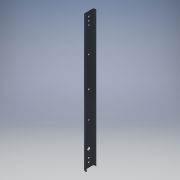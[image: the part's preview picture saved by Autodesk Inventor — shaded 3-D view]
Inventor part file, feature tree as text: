
AUTODESK INVENTOR PART (.ipt)
format: ipt  version: 2016 (Build 200138000, 138)  size: 188,416 bytes
history: native  units: mm
features: sketch x10, extrude x9, other x7, hole x1
ambient origin geometry x8: Origin, YZ Plane, XZ Plane, XY Plane, X Axis, Y Axis, Z Axis, Center Point
bodies: Solid1 (feature_tree)
feature tree (27):
  extrude  "Extrusion1"  Depth=0.5mm TaperAngle=0.0deg
  extrude  "Extrusion2"  Depth=0.5mm TaperAngle=0.0deg
  extrude  "Extrusion3"  Depth=0.5mm TaperAngle=0.0deg
  extrude  "Extrusion4"  Depth=0.5mm TaperAngle=0.0deg
  extrude  "Extrusion5"  [1 undecoded]
  extrude  "Extrusion6"  [1 undecoded]
  extrude  "Extrusion7"  [1 undecoded]
  extrude  "Extrusion8"  [1 undecoded]
  extrude  "Extrusion9"  [1 undecoded]
  hole  "Hole1"  [1 undecoded]
  other  "to_rail_XY"
  other  "to_rail_YZ"
  other  "to_rail_ZX"
  other  "to_rail_X"
  other  "to_rail_Y"
  other  "to_rail_Z"
  other  "to_rail_Center"
  sketch  "Sketch_1"  dims[d0=457.2mm d1=0.0mm d2=0.5mm d3=0.0mm]
  sketch  "Sketch_4"  dims[d8=0.5mm d9=0.0mm d10=0.5mm d11=0.0mm]
  sketch  "Sketch_5"  dims[d12=0.5mm d13=0.0mm d14=0.5mm d15=0.0mm]
  sketch  "Sketch_6"  dims[d16=0.5mm d17=0.0mm]
  sketch  "Sketch_7"  dims[d18=9.5mm d19=6.0mm d20=4.0mm d21=2.0mm d22=90.0deg d23=0.5mm d24=0.0mm]
  sketch  "Sketch_3"  dims[d4=0.5mm d5=0.0mm d6=0.5mm d7=0.0mm]
  sketch  "Sketch_8"
  sketch  "Sketch_9"
  sketch  "Sketch_10"
  sketch  "Sketch10"
note: 6 required parameter values undecoded (feature->parameter linkage not recoverable at this tier; creation-order binding heuristic only, values carry confidence <= 0.55)
